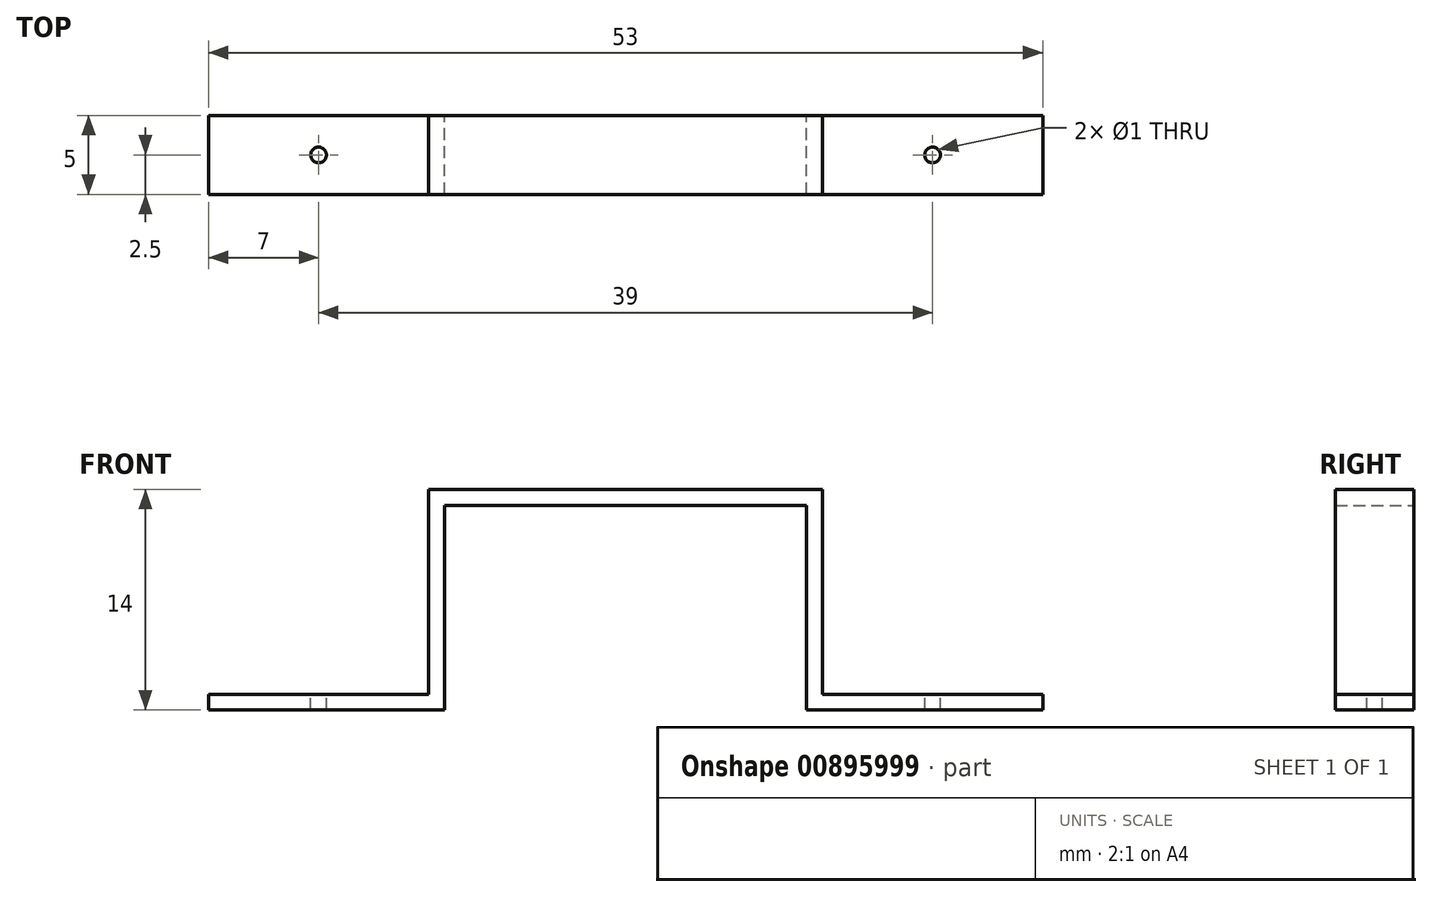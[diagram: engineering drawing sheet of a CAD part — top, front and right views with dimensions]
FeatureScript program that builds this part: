
annotation { "Feature Type Name" : "Feature", "Feature Type Description" : "" }
export const myFeature = defineFeature(function(context is Context, id is Id, definition is map)
    precondition{}
    {
        {
            var Q0;
            Q0=qCreatedBy(makeId("Front.planeOp"),FACE);
            var sketch = newSketch(context, id + "F0", { "sketchPlane" : qUnion([Q0])});
            skLineSegment(sketch, "E0", {"start": v(-11.5, 0) * mm, "end": v(11.5, 0) * mm});
            skLineSegment(sketch, "E1", {"start": v(-11.5, 0) * mm, "end": v(-11.5, -13) * mm});
            skLineSegment(sketch, "E2", {"start": v(-11.5, -13) * mm, "end": v(-26.5, -13) * mm});
            skLineSegment(sketch, "E3", {"start": v(11.5, 0) * mm, "end": v(11.5, -13) * mm});
            skLineSegment(sketch, "E4", {"start": v(11.5, -13) * mm, "end": v(26.5, -13) * mm});
            skLineSegment(sketch, "E5.0", {"start": v(-11.5, 12.2) * mm, "end": v(11.5, 12.2) * mm});
            skLineSegment(sketch, "E6", {"start": v(-26.5, -13) * mm, "end": v(-26.5, -12) * mm});
            skLineSegment(sketch, "E7", {"start": v(-26.5, -12) * mm, "end": v(-12.5, -12) * mm});
            skLineSegment(sketch, "E8", {"start": v(-12.5, -12) * mm, "end": v(-12.5, 1) * mm});
            skLineSegment(sketch, "E9", {"start": v(-12.5, 1) * mm, "end": v(12.5, 1) * mm});
            skLineSegment(sketch, "E10", {"start": v(12.5, 1) * mm, "end": v(12.5, -12) * mm});
            skLineSegment(sketch, "E11", {"start": v(12.5, -12) * mm, "end": v(26.5, -12) * mm});
            skLineSegment(sketch, "E12", {"start": v(26.5, -12) * mm, "end": v(26.5, -13) * mm});
            skSolve(sketch);
        }
        {
            var Q0;
            Q0=makeQuery(id+"F0.imprint","IMPRINT",FACE,{"disambiguationData":[TD([[makeQuery(id+"F0.imprint","IMPRINT",EDGE,{"derivedFrom":sQuery(id+"F0.wireOp",EDGE,"E0")}),1.0]])]});
            extrude(context, id + "F1", {"entities" : qUnion([Q0]), "depth" : 5 * mm, "offsetDistance" : 25 * mm});
        }
        {
            var Q0;
            Q0=makeQuery(id+"F1.opExtrude","SWEPT_FACE",FACE,{"disambiguationData":[OSD([sQuery(id+"F0.wireOp",EDGE,"E7")])]});
            var sketch = newSketch(context, id + "F2", { "sketchPlane" : qUnion([Q0])});
            skLineSegment(sketch, "E13", {"start": v(0, 0) * mm, "end": v(-19.5, 0) * mm, "construction": true});
            skLineSegment(sketch, "E14", {"start": v(-19.5, 0) * mm, "end": v(-19.5, -5) * mm, "construction": true});
            skLineSegment(sketch, "E15", {"start": v(0, 0) * mm, "end": v(19.5, 0) * mm, "construction": true});
            skLineSegment(sketch, "E16", {"start": v(19.5, 0) * mm, "end": v(19.5, -5) * mm, "construction": true});
            skCircle(sketch, "E17", {"center": v(-19.5, -2.5) * mm, "radius": 0.5 * mm});
            skCircle(sketch, "E18", {"center": v(19.5, -2.5) * mm, "radius": 0.5 * mm});
            skSolve(sketch);
        }
        {
            var Q0;
            Q0=makeQuery(id+"F2.imprint","IMPRINT",FACE,{"disambiguationData":[TD([[makeQuery(id+"F2.imprint","IMPRINT",EDGE,{"derivedFrom":sQuery(id+"F2.wireOp",EDGE,"E17")}),1.0]])]});
            var Q1;
            Q1=makeQuery(id+"F2.imprint","IMPRINT",FACE,{"disambiguationData":[TD([[makeQuery(id+"F2.imprint","IMPRINT",EDGE,{"derivedFrom":sQuery(id+"F2.wireOp",EDGE,"E18")}),1.0]])]});
            extrude(context, id + "F3", {"entities" : qUnion([Q0, Q1]), "operationType" : NewBodyOperationType.REMOVE, "endBound" : BoundingType.THROUGH_ALL, "oppositeDirection" : true, "depth" : 25 * mm, "offsetDistance" : 25 * mm});
        }
    });
